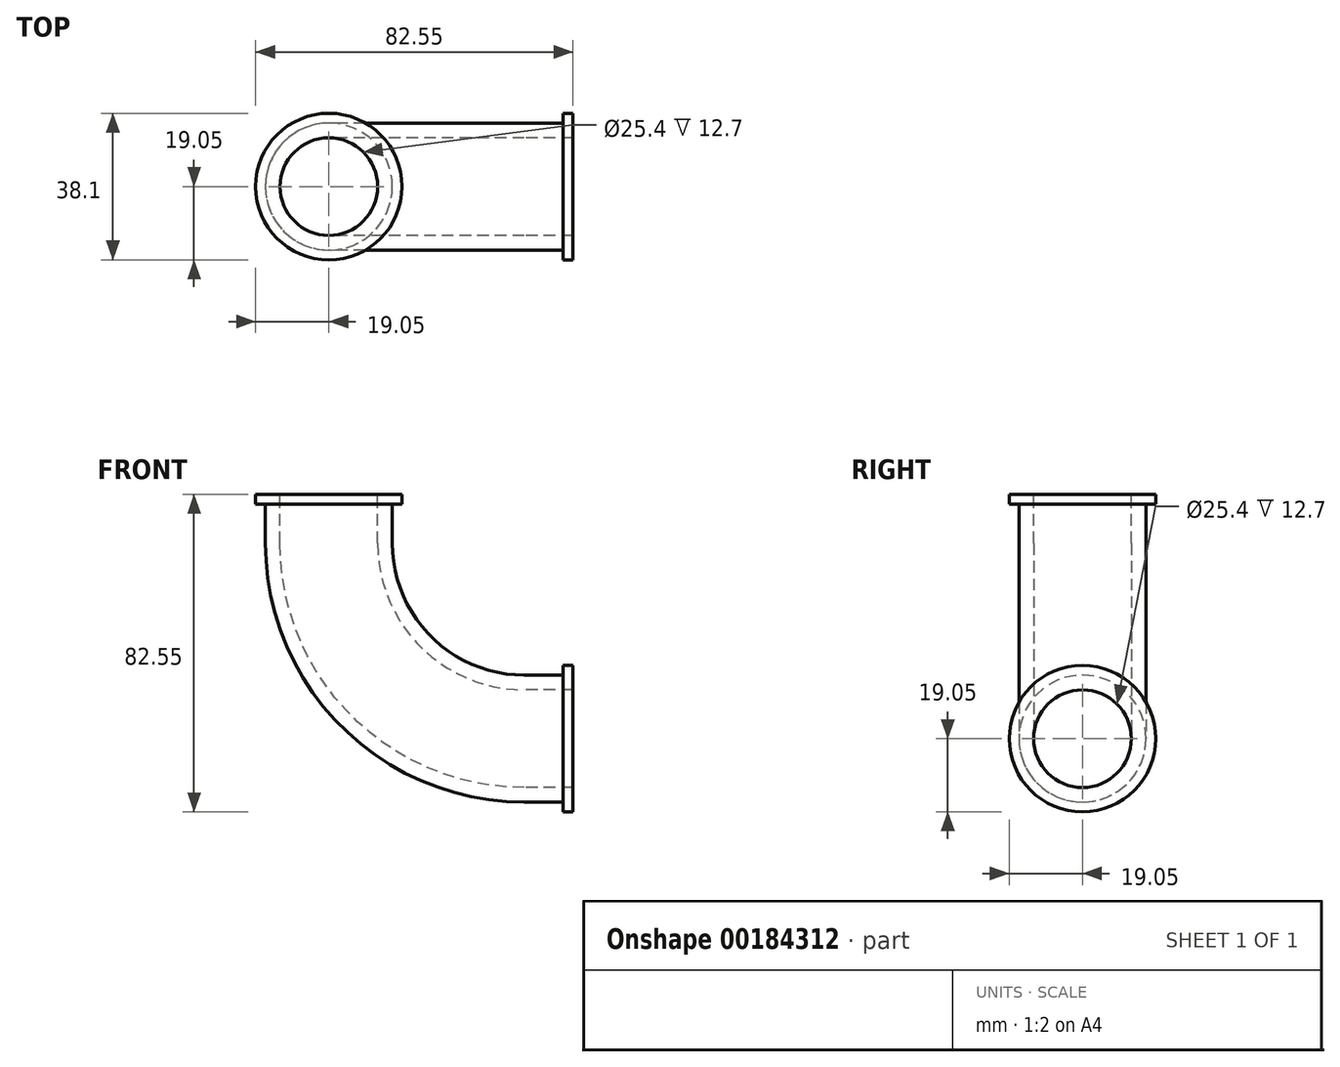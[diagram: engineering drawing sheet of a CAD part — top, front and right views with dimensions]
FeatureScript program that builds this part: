
annotation { "Feature Type Name" : "Feature", "Feature Type Description" : "" }
export const myFeature = defineFeature(function(context is Context, id is Id, definition is map)
    precondition{}
    {
        {
            var Q0;
            Q0=qCreatedBy(makeId("Front.planeOp"),FACE);
            var sketch = newSketch(context, id + "F0", { "sketchPlane" : qUnion([Q0])});
            skArc(sketch, "E0", {"start": v(-50.8, 50.8) * mm, "mid": v(-35.92, 14.88) * mm, "end": v(0, 0) * mm});
            skLineSegment(sketch, "E1", {"start": v(-50.8, 50.8) * mm, "end": v(-50.8, 63.5) * mm});
            skLineSegment(sketch, "E2", {"start": v(0, 0) * mm, "end": v(12.7, 0) * mm});
            skSolve(sketch);
        }
        {
            var Q0;
            Q0=qCreatedBy(makeId("Right.planeOp"),FACE);
            cPlane(context, id + "F1", {"entities" : qUnion([Q0]), "cplaneType" : CPlaneType.OFFSET, "offset" : 12.7 * mm, "width" : 152.4 * mm, "height" : 152.4 * mm});
        }
        {
            var Q0;
            Q0=qCreatedBy(id+"F1.planeOp",FACE);
            var sketch = newSketch(context, id + "F2", { "sketchPlane" : qUnion([Q0])});
            skCircle(sketch, "E3", {"center": v(0, 0) * mm, "radius": 12.7 * mm});
            skCircle(sketch, "E4", {"center": v(0, 0) * mm, "radius": 16.51 * mm});
            skSolve(sketch);
        }
        {
            var Q0;
            Q0=makeQuery(id+"F2.imprint","IMPRINT",FACE,{"disambiguationData":[TD([[makeQuery(id+"F2.imprint","IMPRINT",EDGE,{"derivedFrom":sQuery(id+"F2.wireOp",EDGE,"E3")}),-1.0]])]});
            var Q1;
            Q1=sQuery(id+"F0.wireOp",EDGE,"E2");
            var Q2;
            Q2=sQuery(id+"F0.wireOp",EDGE,"E0");
            var Q3;
            Q3=sQuery(id+"F0.wireOp",EDGE,"E1");
            sweep(context, id + "F3", {"profiles" : qUnion([Q0]), "path" : qUnion([Q1, Q2, Q3])});
        }
        {
            var Q0;
            Q0=makeQuery(id+"F3.opSweep","CAP_FACE",FACE,{"disambiguationData":[OSD([sQuery(id+"F0.wireOp",VERTEX,"E2.end"),sQuery(id+"F2.wireOp",EDGE,"E3"),sQuery(id+"F2.wireOp",EDGE,"E4")])],"isStart":true});
            var sketch = newSketch(context, id + "F4", { "sketchPlane" : qUnion([Q0])});
            skCircle(sketch, "E5", {"center": v(0, 0) * mm, "radius": 19.05 * mm});
            skCircle(sketch, "E6", {"center": v(0, 0) * mm, "radius": 12.7 * mm});
            skSolve(sketch);
        }
        {
            var Q0;
            Q0=qSketchRegion(id+"F4",true);
            extrude(context, id + "F5", {"entities" : qUnion([Q0]), "operationType" : NewBodyOperationType.ADD, "oppositeDirection" : true, "depth" : 2.54 * mm});
        }
        {
            var Q0;
            Q0=makeQuery(id+"F3.opSweep","CAP_FACE",FACE,{"disambiguationData":[OSD([sQuery(id+"F0.wireOp",VERTEX,"E1.end"),sQuery(id+"F2.wireOp",EDGE,"E3"),sQuery(id+"F2.wireOp",EDGE,"E4")])],"isStart":false});
            var sketch = newSketch(context, id + "F6", { "sketchPlane" : qUnion([Q0])});
            skCircle(sketch, "E7", {"center": v(-50.8, 0) * mm, "radius": 12.7 * mm});
            skCircle(sketch, "E8", {"center": v(-50.8, 0) * mm, "radius": 19.05 * mm});
            skSolve(sketch);
        }
        {
            var Q0;
            Q0=qSketchRegion(id+"F6",true);
            extrude(context, id + "F7", {"entities" : qUnion([Q0]), "operationType" : NewBodyOperationType.ADD, "oppositeDirection" : true, "depth" : 2.54 * mm});
        }
    });
